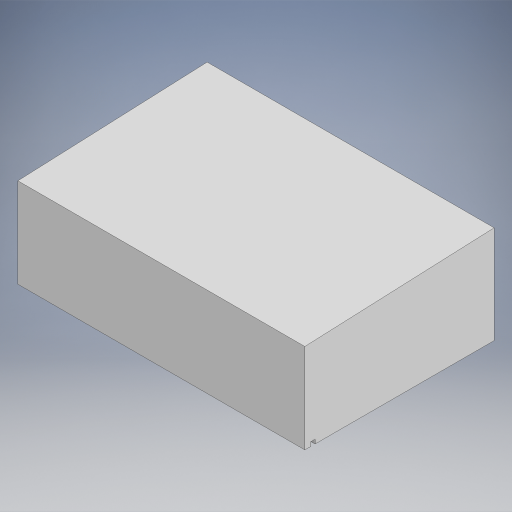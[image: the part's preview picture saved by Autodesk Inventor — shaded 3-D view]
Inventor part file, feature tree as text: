
AUTODESK INVENTOR PART (.ipt)
format: ipt  version: 2023.1 (Build 271208000, 208)  size: 202,752 bytes
history: native  units: in
note: dims shown in document units (in); Inventor stores cm internally (conversion verified against a paired STEP export)
features: extrude x1, sketch x1
ambient origin geometry x8: Origin, YZ Plane, XZ Plane, XY Plane, X Axis, Y Axis, Z Axis, Center Point
bodies: Body1 (feature_tree)
feature tree (2):
  extrude  "Extrusion2"  Depth=11.625in
  sketch  "Sketch2"  dims[d4=6.0in d5=11.625in d6=0.5in d7=0.25in d8=0.25in d9=0.375in d10=17.625in d11=0.0in]
